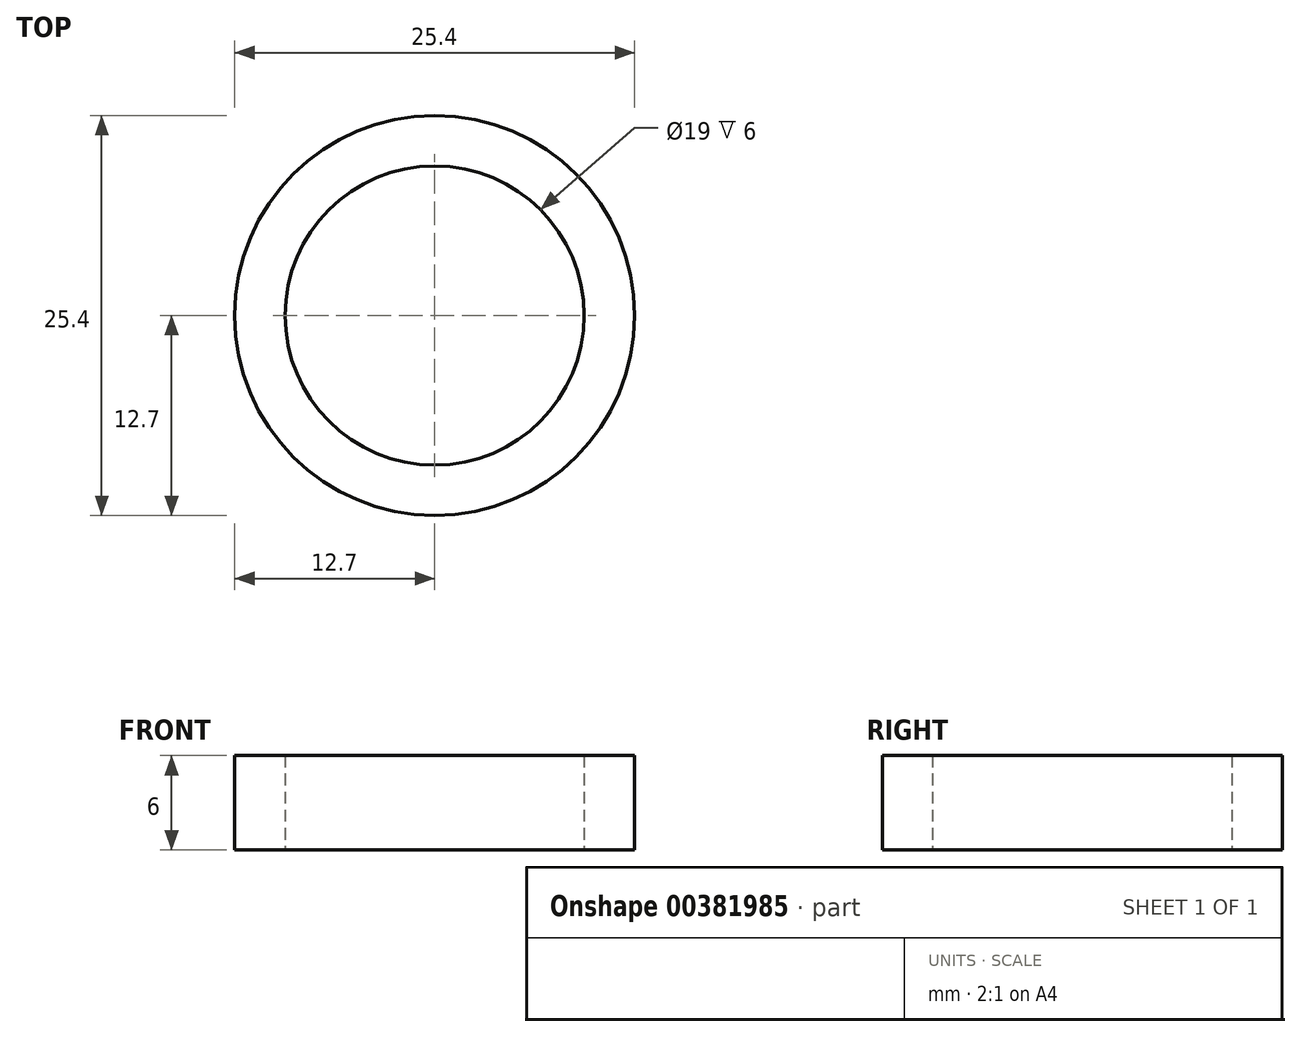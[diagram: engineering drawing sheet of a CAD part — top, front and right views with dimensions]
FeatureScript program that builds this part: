
annotation { "Feature Type Name" : "Feature", "Feature Type Description" : "" }
export const myFeature = defineFeature(function(context is Context, id is Id, definition is map)
    precondition{}
    {
        {
            var Q0;
            Q0=qCreatedBy(makeId("Top.planeOp"),FACE);
            var sketch = newSketch(context, id + "F0", { "sketchPlane" : qUnion([Q0])});
            skCircle(sketch, "E0", {"center": v(0, 0) * mm, "radius": 9.5 * mm});
            skCircle(sketch, "E1.0", {"center": v(0, 0) * mm, "radius": 12.7 * mm});
            skSolve(sketch);
        }
        {
            var Q0;
            Q0=makeQuery(id+"F0.imprint","IMPRINT",FACE,{"disambiguationData":[TD([[makeQuery(id+"F0.imprint","IMPRINT",EDGE,{"derivedFrom":sQuery(id+"F0.wireOp",EDGE,"E0")}),-1.0]])]});
            extrude(context, id + "F1", {"entities" : qUnion([Q0]), "depth" : 6 * mm, "offsetDistance" : 25 * mm});
        }
    });
